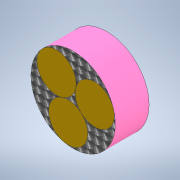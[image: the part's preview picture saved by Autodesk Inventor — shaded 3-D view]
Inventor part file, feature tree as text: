
AUTODESK INVENTOR PART (.ipt)
format: ipt  version: 2021 (Build 250183000, 183)  size: 131,072 bytes
history: native  units: mm
features: extrude x2, sketch x2
ambient origin geometry x8: Origin, YZ Plane, XZ Plane, XY Plane, X Axis, Y Axis, Z Axis, Center Point
bodies: Solid1 (feature_tree)
feature tree (4):
  extrude  "Extrusion1"  Depth=8.0mm TaperAngle=0.0deg
  extrude  "Extrusion2"  [1 undecoded]
  sketch  "Sketch1"  dims[d0=20.0mm d1=8.0mm d2=0.0mm]
  sketch  "Sketch2"  dims[d3=0.01mm d4=0.0mm]
note: 1 required parameter value undecoded (feature->parameter linkage not recoverable at this tier; creation-order binding heuristic only, values carry confidence <= 0.55)
